# Revit family: Electronics_Visual Electronics_ViewSonic_LS900-WU
name_source: partatom
category: Electrical Equipment
revit_build: Autodesk Revit 2017 (Build: 20171027_0315(x64)
units: mm (PartAtom-declared; Revit-internal decimal feet)

## family parameters
Always vertical = Yes
Cut with Voids When Loaded = No
OmniClass Number = 23.80.00.00
OmniClass Title = Electric Power and Lighting
Panel Configuration = Two Columns, Circuits Across
Part Type = Panelboard
Room Calculation Point = No
Round Connector Dimension = Use Diameter
Shared = No
Work Plane-Based = No

## types (1)
- LS900WU
    Assembly Code = D50
    Audible Noise (Eco) = 32dB
    Audible Noise (Normal) = 34dB
    Brightness = 6000 ANSI Lumens
    Contrast Ratio = 3000000:1
    Covering Color = Plastic - ViewSonic - White
    DMD Type = DC3
    Description = LS900WU - 1920 x 1200 Resolution, 6,000 ANSI Lumens, 1.2 - 1.9 Throw Ratio

Bright and versatile for any professional installation, the ViewSonic® LS900WU WUXGA laser projector delivers everything you need for big screens in big venues. Delivering 6,000 lumens of advanced high brightness, 100,000:1 contrast ratio, and up to 30,000 hours* of light source life, this projector is ideal for auditoriums, lecture halls, large boardrooms, houses of worship, and more. Thanks to SuperColor™ technology, content is brought to life with captivating color, crisp graphics, and stunning videos no matter the environment. This top-notch performer is also easy to deploy and manage with its wide 1.65x optical zoom adjustment, vertical/horizontal keystone, 4 corner adjustment, and a vertical/horizontal lens shift feature that provide extreme flexibility in even the most challenging installations. Thanks to the built-in HDBT receiver, the projector is capable of receiving uncompressed HD video and audio from over 200 feet away via network cable. Moreover, 360-degree tilt angle projection, portrait mode, and 24/7 operation allow for extreme mounting flexibility. The ViewSonic® LS900WU is the ideal WUXGA laser projector for professional installations, large venues, and business and education environments.


*Light source life may vary based on actual usage and other factors.
    Diagonal = 1270 mm
    Diagonal (Zoom) = 1270 mm
    Digital Zoom = 1.0x-2.0x
    Display Colour = 1.07 Billion Colours
    Edition number = 1
    HDTV Compatibility = 480i, 480p, 576i, 576p, 720p, 1080i, 1080p
    Height = 675 mm
    Horizontal Frequency = 15K-102KHz
    IAR = 1.5925
    Image Aspect Ratio = / : "16 - 10"
    Image Size = 50"-300"
    Input Lag = 16ms
    Keynote = 16800
    Keystone = H:+/-30° , V:+/-25°
    Lamp Watt = Laser Bank x 4
    Lens = F=2.45-3.13, f=17.23-27.9mm
    Lens Shift H. Range = Yes (+2.5%, -2.5%)
    Lens Shift V. Range = Yes (+9.2%, -2.4%)
    Light Source Life (Normal) = up to 20000
    Light Source Type = Laser Phosphor system
    Manufacturer = ViewSonic
    Model = viewsonic_ls900wu_projector
    Native Resolution = 1920x1200
    Optical Zoom = 1.65x
    Product Guid = a26a97c5-0edd-4c76-ae1f-1bc283295fe4
    Product data url = https://www.bimobject.com
    Projection Distance = 1238 mm
    Projection Offset = 130%+/-10%
    Projection System = 0.67" WUXGA
    Resolution Support = VGA(640 x 480) to WUXGA_RB(1920 x 1200)
*RB-Reduced Blanking
    Throw Distance = 1.24-7.43m (100"@2.48m )
    Throw Ratio = 1.15-1.9
    URL = https://www.viewsonic.com
    Vertical Scan Rate = 23-120Hz
    Video Compatibility = NTSC, PAL, SECAM
    Width = 1076 mm
    Zoom = 1
    Zoom Control = 1
    a = / : "4  - 3"
    b = / : "16 - 9"
    c = / : "16 - 10"

## geometry (parser evidence)
native form markers: Sweep x9
no freeform markers — native parametric forms only
